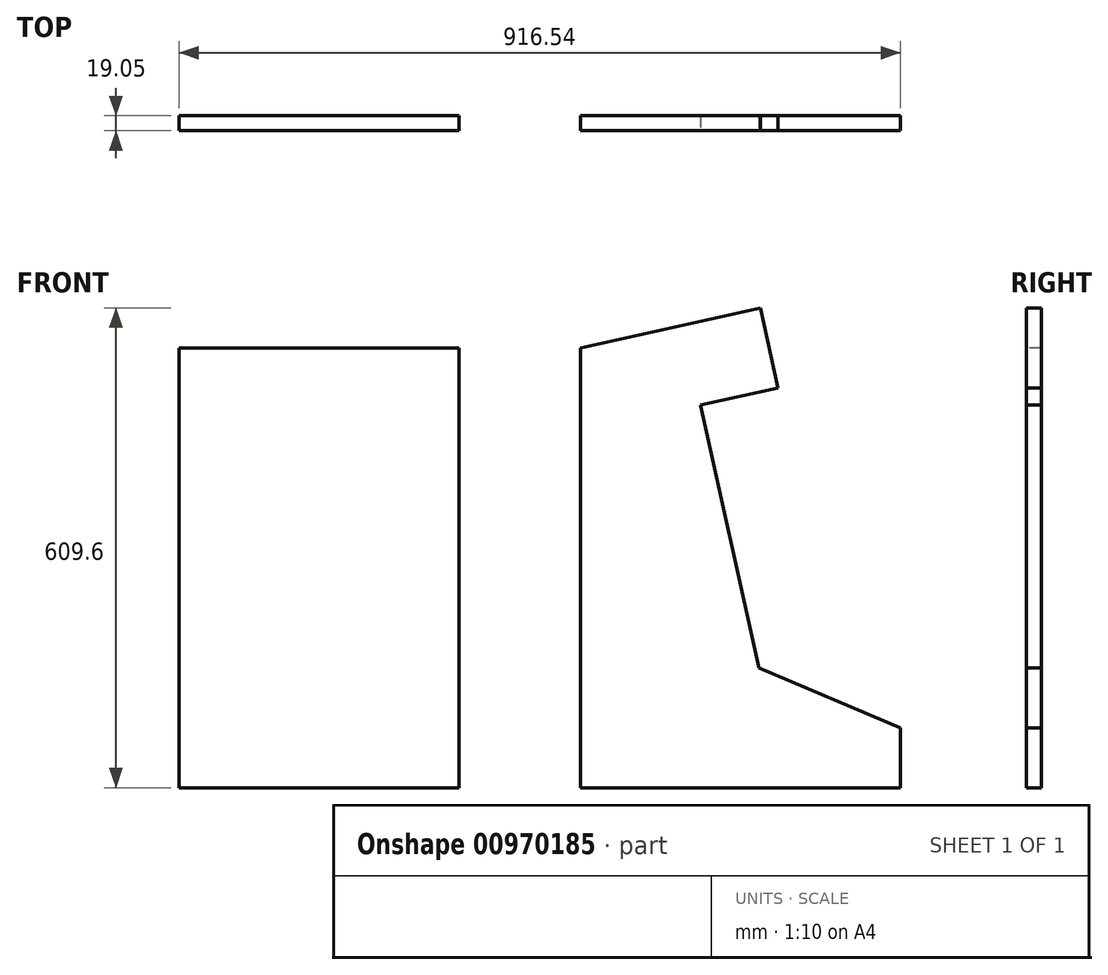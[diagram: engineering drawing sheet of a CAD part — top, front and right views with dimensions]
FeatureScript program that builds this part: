
annotation { "Feature Type Name" : "Feature", "Feature Type Description" : "" }
export const myFeature = defineFeature(function(context is Context, id is Id, definition is map)
    precondition{}
    {
        {
            var Q0;
            Q0=qCreatedBy(makeId("Front.planeOp"),FACE);
            var sketch = newSketch(context, id + "F0", { "sketchPlane" : qUnion([Q0])});
            skLineSegment(sketch, "E0.bottom", {"start": v(0, 0) * mm, "end": v(355.6, 0) * mm});
            skLineSegment(sketch, "E0.top", {"start": v(0, 609.6) * mm, "end": v(355.6, 609.6) * mm});
            skLineSegment(sketch, "E0.left", {"start": v(0, 0) * mm, "end": v(0, 609.6) * mm});
            skLineSegment(sketch, "E0.right", {"start": v(355.6, 0) * mm, "end": v(355.6, 609.6) * mm});
            skSolve(sketch);
        }
        {
            var Q0;
            Q0 = qSketchRegion(id + "F0", true);
            extrude(context, id + "F1", {"entities" : qUnion([Q0]), "depth" : 19.05 * mm, "offsetDistance" : 25.4 * mm});
        }
        {
            var Q0;
            Q0=qCreatedBy(makeId("Front.planeOp"),FACE);
            var sketch = newSketch(context, id + "F2", { "sketchPlane" : qUnion([Q0])});
            skLineSegment(sketch, "E1.bottom", {"start": v(510.14, 0) * mm, "end": v(916.54, 0) * mm});
            skLineSegment(sketch, "E1.top", {"start": v(510.14, 609.6) * mm, "end": v(916.54, 609.6) * mm});
            skLineSegment(sketch, "E1.left", {"start": v(510.14, 0) * mm, "end": v(510.14, 609.6) * mm});
            skLineSegment(sketch, "E1.right", {"start": v(916.54, 0) * mm, "end": v(916.54, 609.6) * mm});
            skSolve(sketch);
        }
        {
            var Q0;
            Q0 = qSketchRegion(id + "F2", true);
            extrude(context, id + "F3", {"entities" : qUnion([Q0]), "depth" : 19.05 * mm, "offsetDistance" : 25.4 * mm});
        }
        {
            var Q0;
            Q0=makeQuery(id+"F3.opExtrude","CAP_FACE",FACE,{"disambiguationData":[OSD([sQuery(id+"F2.wireOp",EDGE,"E1.bottom"),sQuery(id+"F2.wireOp",EDGE,"E1.top"),sQuery(id+"F2.wireOp",EDGE,"E1.left"),sQuery(id+"F2.wireOp",EDGE,"E1.right")])],"isStart":false});
            var sketch = newSketch(context, id + "F4", { "sketchPlane" : qUnion([Q0])});
            skLineSegment(sketch, "E2", {"start": v(738.74, 609.6) * mm, "end": v(510.14, 558.8) * mm});
            skLineSegment(sketch, "E3", {"start": v(662.54, 486.05) * mm, "end": v(736.69, 152.4) * mm});
            skLineSegment(sketch, "E4", {"start": v(736.69, 152.4) * mm, "end": v(916.54, 76.2) * mm});
            skLineSegment(sketch, "E5", {"start": v(738.74, 609.6) * mm, "end": v(761.32, 508) * mm});
            skLineSegment(sketch, "E6", {"start": v(761.32, 508) * mm, "end": v(662.54, 486.05) * mm});
            skLineSegment(sketch, "E7", {"start": v(510.14, 558.8) * mm, "end": v(510.14, 609.6) * mm});
            skLineSegment(sketch, "E8", {"start": v(510.14, 609.6) * mm, "end": v(916.54, 609.6) * mm});
            skLineSegment(sketch, "E9", {"start": v(916.54, 609.6) * mm, "end": v(916.54, 76.2) * mm});
            skSolve(sketch);
        }
        {
            var Q0;
            Q0=makeQuery(id+"F4.imprint","IMPRINT",FACE,{"disambiguationData":[TD([[makeQuery(id+"F4.imprint","IMPRINT",EDGE,{"derivedFrom":sQuery(id+"F4.wireOp",EDGE,"E3")}),1.0]])]});
            var Q1;
            {var subQ0=sQuery(id+"F4.wireOp",EDGE,"E2");Q1=makeQuery(id+"F4.imprint","IMPRINT",FACE,{"disambiguationData":[TD([[makeQuery(id+"F4.imprint","IMPRINT",EDGE,{"derivedFrom":subQ0}),-1.0]])]});}
            extrude(context, id + "F5", {"entities" : qUnion([Q0, Q1]), "operationType" : NewBodyOperationType.REMOVE, "endBound" : BoundingType.THROUGH_ALL, "oppositeDirection" : true, "depth" : 25.4 * mm, "offsetDistance" : 25.4 * mm});
        }
        {
            var Q0;
            Q0=makeQuery(id+"F1.opExtrude","CAP_FACE",FACE,{"disambiguationData":[OSD([sQuery(id+"F0.wireOp",EDGE,"E0.bottom"),sQuery(id+"F0.wireOp",EDGE,"E0.top"),sQuery(id+"F0.wireOp",EDGE,"E0.left"),sQuery(id+"F0.wireOp",EDGE,"E0.right")])],"isStart":false});
            var sketch = newSketch(context, id + "F6", { "sketchPlane" : qUnion([Q0])});
            skLineSegment(sketch, "E10.bottom", {"start": v(0, 609.6) * mm, "end": v(355.6, 609.6) * mm});
            skLineSegment(sketch, "E10.top", {"start": v(0, 558.8) * mm, "end": v(355.6, 558.8) * mm});
            skLineSegment(sketch, "E10.left", {"start": v(0, 609.6) * mm, "end": v(0, 558.8) * mm});
            skLineSegment(sketch, "E10.right", {"start": v(355.6, 609.6) * mm, "end": v(355.6, 558.8) * mm});
            skSolve(sketch);
        }
        {
            var Q0;
            Q0 = qSketchRegion(id + "F6", true);
            extrude(context, id + "F7", {"entities" : qUnion([Q0]), "operationType" : NewBodyOperationType.REMOVE, "endBound" : BoundingType.THROUGH_ALL, "oppositeDirection" : true, "depth" : 25.4 * mm, "offsetDistance" : 25.4 * mm});
        }
    });
